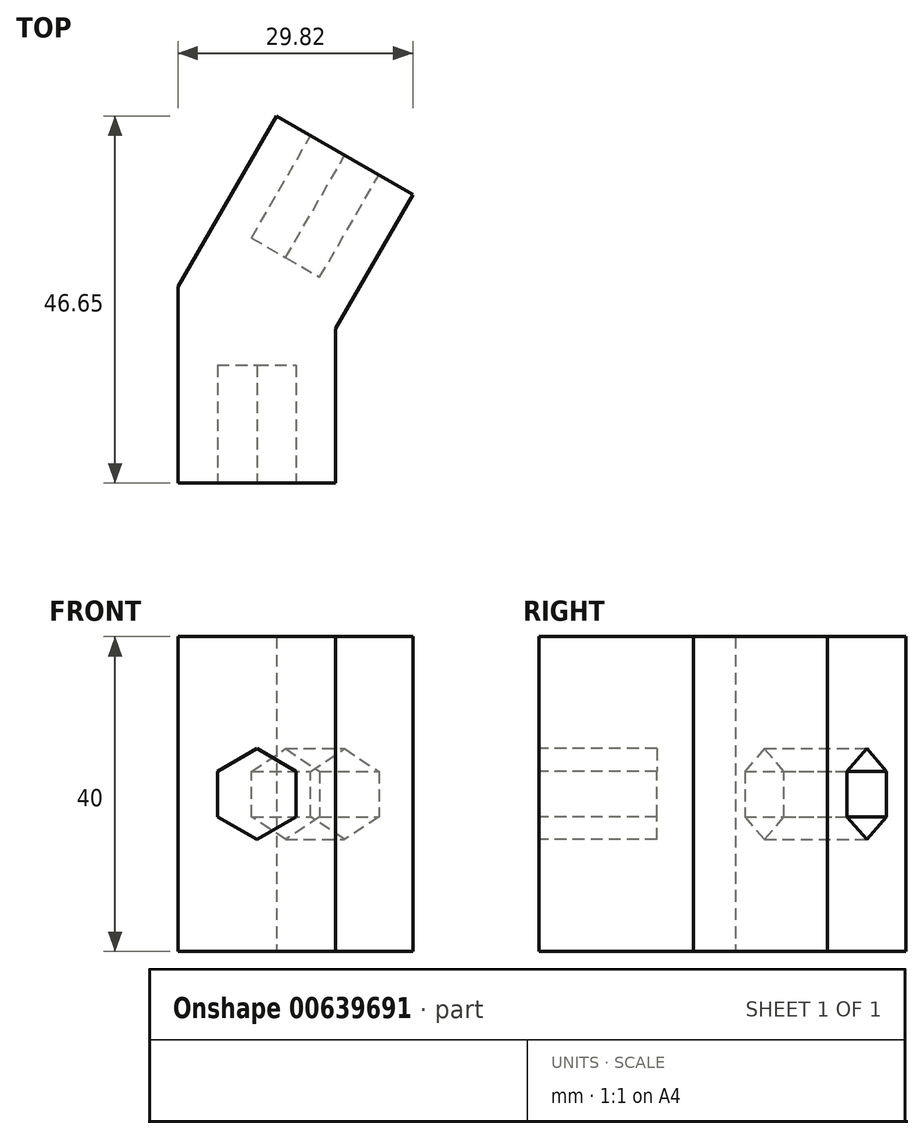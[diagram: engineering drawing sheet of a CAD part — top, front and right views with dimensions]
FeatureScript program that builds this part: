
annotation { "Feature Type Name" : "Feature", "Feature Type Description" : "" }
export const myFeature = defineFeature(function(context is Context, id is Id, definition is map)
    precondition{}
    {
        {
            var Q0;
            Q0=qCreatedBy(makeId("Front.planeOp"),FACE);
            var sketch = newSketch(context, id + "F0", { "sketchPlane" : qUnion([Q0])});
            skLineSegment(sketch, "E0.bottom", {"start": v(10, 20) * mm, "end": v(-10, 20) * mm});
            skLineSegment(sketch, "E0.top", {"start": v(10, -20) * mm, "end": v(-10, -20) * mm});
            skLineSegment(sketch, "E0.left", {"start": v(10, 20) * mm, "end": v(10, -20) * mm});
            skLineSegment(sketch, "E0.right", {"start": v(-10, 20) * mm, "end": v(-10, -20) * mm});
            skPoint(sketch, "E0.middle", {"position": v(0, 0) * mm});
            skLineSegment(sketch, "E1", {"start": v(0, 0) * mm, "end": v(0, 20) * mm});
            skSolve(sketch);
        }
        {
            var Q0;
            Q0 = qSketchRegion(id + "F0", true);
            extrude(context, id + "F1", {"entities" : qUnion([Q0]), "depth" : 25 * mm, "offsetDistance" : 25 * mm});
        }
        {
            var Q0;
            Q0=makeQuery(id+"F1.opExtrude","CAP_FACE",FACE,{"disambiguationData":[OSD([sQuery(id+"F0.wireOp",EDGE,"E0.bottom"),sQuery(id+"F0.wireOp",EDGE,"E0.top"),sQuery(id+"F0.wireOp",EDGE,"E0.left"),sQuery(id+"F0.wireOp",EDGE,"E0.right")])],"isStart":true});
            var Q1;
            Q1=makeQuery(id+"F1.opExtrude","CAP_EDGE",EDGE,{"disambiguationData":[OSD([sQuery(id+"F0.wireOp",EDGE,"E0.right")])],"isStart":true});
            cPlane(context, id + "F2", {"entities" : qUnion([Q0, Q1]), "cplaneType" : CPlaneType.LINE_ANGLE, "offset" : 25 * mm, "angle" : 15 * degree, "width" : 150 * mm, "height" : 150 * mm});
        }
        {
            var Q0;
            Q0=makeQuery(id+"F1.opExtrude","CAP_FACE",FACE,{"disambiguationData":[OSD([sQuery(id+"F0.wireOp",EDGE,"E0.bottom"),sQuery(id+"F0.wireOp",EDGE,"E0.top"),sQuery(id+"F0.wireOp",EDGE,"E0.left"),sQuery(id+"F0.wireOp",EDGE,"E0.right")])],"isStart":false});
            var Q1;
            Q1 = qBodyType(qCreatedBy(id + "F4" ,EDGE), BodyType.WIRE);
            cPlane(context, id + "F3", {"entities" : qUnion([Q0, Q1]), "cplaneType" : CPlaneType.OFFSET, "offset" : 0 * mm, "width" : 150 * mm, "height" : 150 * mm});
        }
        {
            var Q0;
            Q0=qCreatedBy(id+"F3.planeOp",FACE);
            var sketch = newSketch(context, id + "F4", { "sketchPlane" : qUnion([Q0])});
            skCircle(sketch, "E2.cCircle", {"center": v(0, 0) * mm, "radius": 5 * mm, "construction": true});
            skLineSegment(sketch, "E2.0", {"start": v(0, 5.77) * mm, "end": v(5, 2.89) * mm});
            skLineSegment(sketch, "E2.1", {"start": v(5, 2.89) * mm, "end": v(5, -2.89) * mm});
            skLineSegment(sketch, "E2.2", {"start": v(5, -2.89) * mm, "end": v(0, -5.77) * mm});
            skLineSegment(sketch, "E2.3", {"start": v(0, -5.77) * mm, "end": v(-5, -2.89) * mm});
            skLineSegment(sketch, "E2.4", {"start": v(-5, -2.89) * mm, "end": v(-5, 2.89) * mm});
            skLineSegment(sketch, "E2.5", {"start": v(-5, 2.89) * mm, "end": v(0, 5.77) * mm});
            skPoint(sketch, "E2.0.midPoint", {"position": v(2.5, 4.33) * mm});
            skSolve(sketch);
        }
        {
            var Q0;
            Q0 = qSketchRegion(id + "F4", true);
            extrude(context, id + "F5", {"entities" : qUnion([Q0]), "operationType" : NewBodyOperationType.REMOVE, "oppositeDirection" : true, "depth" : 15 * mm, "offsetDistance" : 25 * mm});
        }
        {
            var Q0;
            Q0=makeQuery(id+"F1.opExtrude","SWEPT_BODY",BODY,{"disambiguationData":[OSD([sQuery(id+"F0.wireOp",EDGE,"E0.bottom"),sQuery(id+"F0.wireOp",EDGE,"E0.top"),sQuery(id+"F0.wireOp",EDGE,"E0.left"),sQuery(id+"F0.wireOp",EDGE,"E0.right")])]});
            var Q1;
            Q1=qCreatedBy(id+"F2.planeOp",FACE);
            mirror(context, id + "F6", {"operationType" : NewBodyOperationType.ADD, "entities" : qUnion([Q0]), "mirrorPlane" : qUnion([Q1])});
        }
    });
